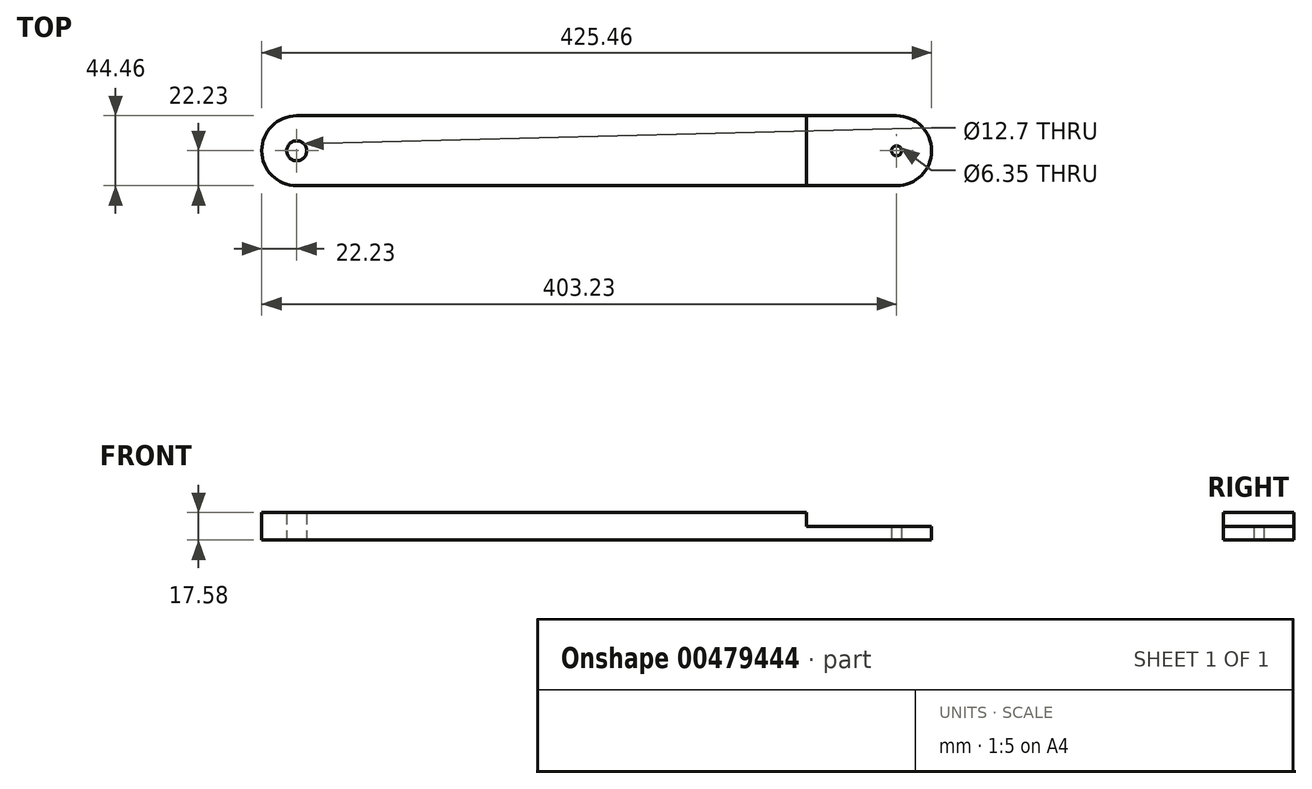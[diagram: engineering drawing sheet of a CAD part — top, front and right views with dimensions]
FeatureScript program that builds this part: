
annotation { "Feature Type Name" : "Feature", "Feature Type Description" : "" }
export const myFeature = defineFeature(function(context is Context, id is Id, definition is map)
    precondition{}
    {
        {
            var Q0;
            Q0=qCreatedBy(makeId("Top.planeOp"),FACE);
            var sketch = newSketch(context, id + "F0", { "sketchPlane" : qUnion([Q0]), "disableImprinting" : false});
            skCircle(sketch, "E0", {"center": v(0, 0) * mm, "radius": 22.23 * mm});
            skCircle(sketch, "E1", {"center": v(381, 0) * mm, "radius": 22.23 * mm});
            skLineSegment(sketch, "E2", {"start": v(0, 22.23) * mm, "end": v(381, 22.23) * mm});
            skLineSegment(sketch, "E3", {"start": v(0, -22.23) * mm, "end": v(381, -22.23) * mm});
            skCircle(sketch, "E4", {"center": v(0, 0) * mm, "radius": 6.35 * mm});
            skCircle(sketch, "E5", {"center": v(381, 0) * mm, "radius": 3.18 * mm});
            skLineSegment(sketch, "E6", {"start": v(323.85, 22.23) * mm, "end": v(323.85, -22.23) * mm});
            skSolve(sketch);
        }
        {
            var Q0;
            Q0=makeQuery(id+"F0.imprint","IMPRINT",FACE,{"disambiguationData":[TD([[makeQuery(id+"F0.imprint","IMPRINT",EDGE,{"derivedFrom":sQuery(id+"F0.wireOp",EDGE,"E4")}),-1.0]])]});
            var Q1;
            {var subQ5=sQuery(id+"F0.wireOp",EDGE,"E6");Q1=makeQuery(id+"F0.imprint","IMPRINT",FACE,{"disambiguationData":[TD([[makeQuery(id+"F0.imprint","IMPRINT",EDGE,{"derivedFrom":subQ5}),-1.0]])]});}
            extrude(context, id + "F1", {"entities" : qUnion([Q0, Q1]), "depth" : 17.58 * mm});
        }
        {
            var Q0;
            Q0=makeQuery(id+"F0.imprint","IMPRINT",FACE,{"disambiguationData":[TD([[makeQuery(id+"F0.imprint","IMPRINT",EDGE,{"derivedFrom":sQuery(id+"F0.wireOp",EDGE,"E5")}),-1.0]])]});
            var Q1;
            {var subQ5=sQuery(id+"F0.wireOp",EDGE,"E6");Q1=makeQuery(id+"F0.imprint","IMPRINT",FACE,{"disambiguationData":[TD([[makeQuery(id+"F0.imprint","IMPRINT",EDGE,{"derivedFrom":subQ5}),1.0]])]});}
            extrude(context, id + "F2", {"entities" : qUnion([Q0, Q1]), "operationType" : NewBodyOperationType.ADD, "depth" : 8.79 * mm});
        }
    });
